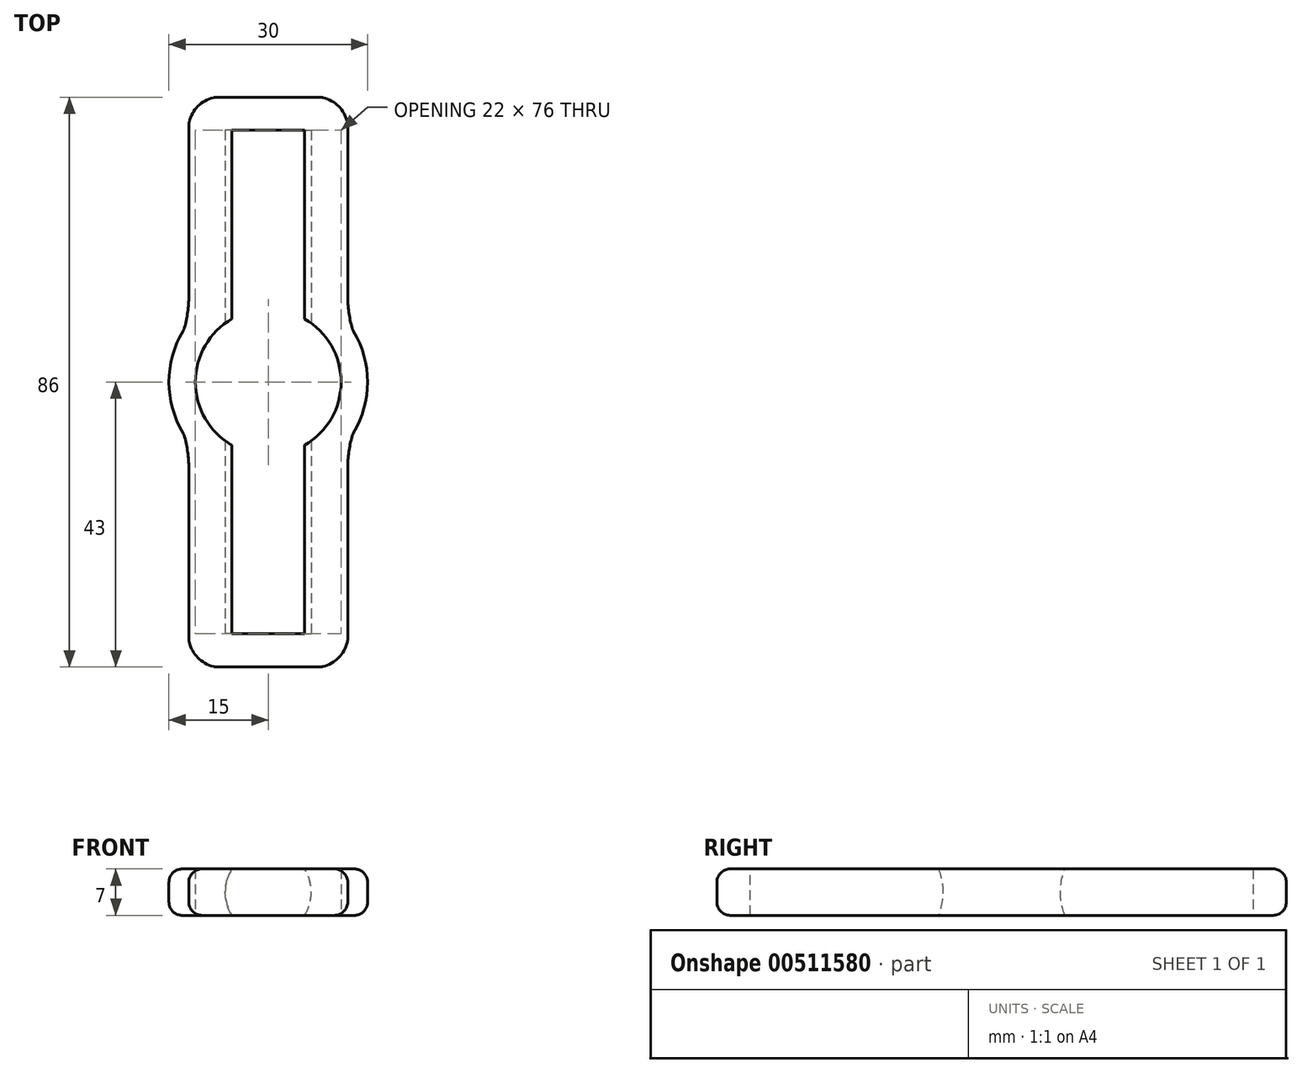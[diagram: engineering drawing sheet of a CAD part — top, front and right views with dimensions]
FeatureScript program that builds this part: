
annotation { "Feature Type Name" : "Feature", "Feature Type Description" : "" }
export const myFeature = defineFeature(function(context is Context, id is Id, definition is map)
    precondition{}
    {
        {
            var Q0;
            Q0=qCreatedBy(makeId("Top.planeOp"),FACE);
            var sketch = newSketch(context, id + "F0", { "sketchPlane" : qUnion([Q0])});
            skCircle(sketch, "E0", {"center": v(0, 0) * mm, "radius": 11 * mm});
            skCircle(sketch, "E1.0", {"center": v(0, 0) * mm, "radius": 15 * mm});
            skLineSegment(sketch, "E2", {"start": v(0, 11) * mm, "end": v(0, 15) * mm});
            skLineSegment(sketch, "E3", {"start": v(-12, 13) * mm, "end": v(-12, 39) * mm});
            skLineSegment(sketch, "E4", {"start": v(12, 13) * mm, "end": v(12, 39) * mm});
            skLineSegment(sketch, "E5", {"start": v(-8, 43) * mm, "end": v(-4, 43) * mm});
            skArc(sketch, "E6", {"start": v(-12.74, 7.92) * mm, "mid": v(-12.19, 10.43) * mm, "end": v(-12, 13) * mm});
            skArc(sketch, "E7.MirrorCS", {"start": v(12.74, 7.92) * mm, "mid": v(12.19, 10.43) * mm, "end": v(12, 13) * mm});
            skPoint(sketch, "E8.orphan", {"position": v(0, 13) * mm});
            skLineSegment(sketch, "E9.MirrorCS", {"start": v(12, -13) * mm, "end": v(12, -39) * mm});
            skLineSegment(sketch, "E10.MirrorCS", {"start": v(-8, -43) * mm, "end": v(8, -43) * mm});
            skLineSegment(sketch, "E11.MirrorCS", {"start": v(-12, -13) * mm, "end": v(-12, -39) * mm});
            skArc(sketch, "E12.MirrorCS", {"start": v(12.74, -7.92) * mm, "mid": v(12.19, -10.43) * mm, "end": v(12, -13) * mm});
            skArc(sketch, "E13.MirrorCS", {"start": v(-12.74, -7.92) * mm, "mid": v(-12.19, -10.43) * mm, "end": v(-12, -13) * mm});
            skLineSegment(sketch, "E14", {"start": v(4, 43) * mm, "end": v(4, 14.46) * mm});
            skPoint(sketch, "E15.start.orphan", {"position": v(0, 50.01) * mm});
            skLineSegment(sketch, "E16.MirrorCS", {"start": v(-4, 43) * mm, "end": v(-4, 14.46) * mm});
            skLineSegment(sketch, "E17.MirrorCS", {"start": v(-4, -43) * mm, "end": v(-4, -14.46) * mm});
            skLineSegment(sketch, "E18.MirrorCS", {"start": v(4, -43) * mm, "end": v(4, -14.46) * mm});
            skLineSegment(sketch, "E19.trimOffspring", {"start": v(4, 43) * mm, "end": v(8, 43) * mm});
            skPoint(sketch, "E20", {"position": v(8, 43) * mm});
            skPoint(sketch, "E21", {"position": v(12, 39) * mm});
            skArc(sketch, "E22", {"start": v(12, 39) * mm, "mid": v(10.62, 41.62) * mm, "end": v(8, 43) * mm});
            skPoint(sketch, "E23.orphan", {"position": v(12, 43) * mm});
            skArc(sketch, "E24.MirrorCS", {"start": v(-12, 39) * mm, "mid": v(-10.62, 41.62) * mm, "end": v(-8, 43) * mm});
            skArc(sketch, "E25.MirrorCS", {"start": v(12, -39) * mm, "mid": v(10.62, -41.62) * mm, "end": v(8, -43) * mm});
            skArc(sketch, "E26.MirrorCS", {"start": v(-12, -39) * mm, "mid": v(-10.62, -41.62) * mm, "end": v(-8, -43) * mm});
            skPoint(sketch, "E27.orphan", {"position": v(-12, 43) * mm});
            skPoint(sketch, "E28.orphan", {"position": v(12, -43) * mm});
            skPoint(sketch, "E29.orphan", {"position": v(-12, -43) * mm});
            skLineSegment(sketch, "E30", {"start": v(-4, 43) * mm, "end": v(4, 43) * mm});
            skSolve(sketch);
        }
        {
            var Q0;
            {var subQ1=sQuery(id+"F0.wireOp",EDGE,"E3");Q0=makeQuery(id+"F0.imprint","IMPRINT",FACE,{"disambiguationData":[TD([[makeQuery(id+"F0.imprint","IMPRINT",EDGE,{"derivedFrom":subQ1}),-1.0]])]});}
            var Q1;
            {var subQ1=sQuery(id+"F0.wireOp",EDGE,"E4");Q1=makeQuery(id+"F0.imprint","IMPRINT",FACE,{"disambiguationData":[TD([[makeQuery(id+"F0.imprint","IMPRINT",EDGE,{"derivedFrom":subQ1}),1.0]])]});}
            var Q2;
            {var subQ0=sQuery(id+"F0.wireOp",EDGE,"E14");Q2=makeQuery(id+"F0.imprint","IMPRINT",FACE,{"disambiguationData":[TD([[makeQuery(id+"F0.imprint","IMPRINT",EDGE,{"derivedFrom":subQ0}),-1.0]])]});}
            var Q3;
            Q3=makeQuery(id+"F0.imprint","IMPRINT",FACE,{"disambiguationData":[TD([[makeQuery(id+"F0.imprint","IMPRINT",EDGE,{"derivedFrom":sQuery(id+"F0.wireOp",EDGE,"E0")}),-1.0]])]});
            var Q4;
            {var subQ1=sQuery(id+"F0.wireOp",EDGE,"E9.MirrorCS");Q4=makeQuery(id+"F0.imprint","IMPRINT",FACE,{"disambiguationData":[TD([[makeQuery(id+"F0.imprint","IMPRINT",EDGE,{"derivedFrom":subQ1}),-1.0]])]});}
            var Q5;
            {var subQ0=sQuery(id+"F0.wireOp",EDGE,"E17.MirrorCS");Q5=makeQuery(id+"F0.imprint","IMPRINT",FACE,{"disambiguationData":[TD([[makeQuery(id+"F0.imprint","IMPRINT",EDGE,{"derivedFrom":subQ0}),-1.0]])]});}
            var Q6;
            {var subQ1=sQuery(id+"F0.wireOp",EDGE,"E11.MirrorCS");Q6=makeQuery(id+"F0.imprint","IMPRINT",FACE,{"disambiguationData":[TD([[makeQuery(id+"F0.imprint","IMPRINT",EDGE,{"derivedFrom":subQ1}),1.0]])]});}
            extrude(context, id + "F1", {"entities" : qUnion([Q0, Q1, Q2, Q3, Q4, Q5, Q6]), "endBound" : BoundingType.SYMMETRIC, "depth" : 7 * mm});
        }
        {
            var Q0;
            Q0=qCreatedBy(makeId("Front.planeOp"),FACE);
            var sketch = newSketch(context, id + "F2", { "sketchPlane" : qUnion([Q0])});
            skCircle(sketch, "E31", {"center": v(0, 0) * mm, "radius": 6.5 * mm});
            skSolve(sketch);
        }
        {
            var Q0;
            Q0=makeQuery(id+"F2.imprint","IMPRINT",FACE,{"disambiguationData":[TD([[makeQuery(id+"F2.imprint","IMPRINT",EDGE,{"derivedFrom":sQuery(id+"F2.wireOp",EDGE,"E31")}),1.0]])]});
            extrude(context, id + "F3", {"entities" : qUnion([Q0]), "operationType" : NewBodyOperationType.REMOVE, "endBound" : BoundingType.SYMMETRIC, "oppositeDirection" : true, "depth" : 76 * mm});
        }
        {
            var Q0;
            Q0=makeQuery(id+"F1.opExtrude","SWEPT_FACE",FACE,{"disambiguationData":[OSD([sQuery(id+"F0.wireOp",EDGE,"E3")])]});
            var Q1;
            Q1=makeQuery(id+"F1.opExtrude","SWEPT_FACE",FACE,{"disambiguationData":[OSD([sQuery(id+"F0.wireOp",EDGE,"E6")])]});
            var Q2;
            {var subQ0=sQuery(id+"F0.wireOp",EDGE,"E1.0");Q2=makeQuery(id+"F1.opExtrude","SWEPT_FACE",FACE,{"disambiguationData":[OSD([subQ0]),TDD([makeQuery(id+"F0.imprint","IMPRINT",EDGE,{"disambiguationData":[TD([[makeQuery(id+"F0.imprint","INTERSECT",VERTEX,{"derivedFrom":[subQ0,sQuery(id+"F0.wireOp",EDGE,"E6")]}),-1.0]])],"derivedFrom":subQ0})])]});}
            var Q3;
            Q3=makeQuery(id+"F1.opExtrude","SWEPT_FACE",FACE,{"disambiguationData":[OSD([sQuery(id+"F0.wireOp",EDGE,"E13.MirrorCS")])]});
            var Q4;
            Q4=makeQuery(id+"F1.opExtrude","SWEPT_FACE",FACE,{"disambiguationData":[OSD([sQuery(id+"F0.wireOp",EDGE,"E11.MirrorCS")])]});
            var Q5;
            Q5=makeQuery(id+"F1.opExtrude","SWEPT_FACE",FACE,{"disambiguationData":[OSD([sQuery(id+"F0.wireOp",EDGE,"E26.MirrorCS")])]});
            var Q6;
            Q6=makeQuery(id+"F1.opExtrude","SWEPT_FACE",FACE,{"disambiguationData":[OSD([sQuery(id+"F0.wireOp",EDGE,"E10.MirrorCS")])]});
            var Q7;
            Q7=makeQuery(id+"F1.opExtrude","SWEPT_FACE",FACE,{"disambiguationData":[OSD([sQuery(id+"F0.wireOp",EDGE,"E25.MirrorCS")])]});
            var Q8;
            Q8=makeQuery(id+"F1.opExtrude","SWEPT_FACE",FACE,{"disambiguationData":[OSD([sQuery(id+"F0.wireOp",EDGE,"E9.MirrorCS")])]});
            var Q9;
            Q9=makeQuery(id+"F1.opExtrude","SWEPT_FACE",FACE,{"disambiguationData":[OSD([sQuery(id+"F0.wireOp",EDGE,"E12.MirrorCS")])]});
            var Q10;
            {var subQ0=sQuery(id+"F0.wireOp",EDGE,"E1.0");Q10=makeQuery(id+"F1.opExtrude","SWEPT_FACE",FACE,{"disambiguationData":[OSD([subQ0]),TDD([makeQuery(id+"F0.imprint","IMPRINT",EDGE,{"disambiguationData":[TD([[makeQuery(id+"F0.imprint","INTERSECT",VERTEX,{"derivedFrom":[subQ0,sQuery(id+"F0.wireOp",EDGE,"E7.MirrorCS")]}),1.0]])],"derivedFrom":subQ0})])]});}
            var Q11;
            Q11=makeQuery(id+"F1.opExtrude","SWEPT_FACE",FACE,{"disambiguationData":[OSD([sQuery(id+"F0.wireOp",EDGE,"E7.MirrorCS")])]});
            var Q12;
            Q12=makeQuery(id+"F1.opExtrude","SWEPT_FACE",FACE,{"disambiguationData":[OSD([sQuery(id+"F0.wireOp",EDGE,"E4")])]});
            var Q13;
            Q13=makeQuery(id+"F1.opExtrude","SWEPT_FACE",FACE,{"disambiguationData":[OSD([sQuery(id+"F0.wireOp",EDGE,"E22")])]});
            var Q14;
            Q14=makeQuery(id+"F1.opExtrude","SWEPT_FACE",FACE,{"disambiguationData":[OSD([sQuery(id+"F0.wireOp",EDGE,"E5"),sQuery(id+"F0.wireOp",EDGE,"E19.trimOffspring"),sQuery(id+"F0.wireOp",EDGE,"E30")])]});
            var Q15;
            Q15=makeQuery(id+"F1.opExtrude","SWEPT_FACE",FACE,{"disambiguationData":[OSD([sQuery(id+"F0.wireOp",EDGE,"E24.MirrorCS")])]});
            fillet(context, id + "F4", {"entities" : qUnion([Q0, Q1, Q2, Q3, Q4, Q5, Q6, Q7, Q8, Q9, Q10, Q11, Q12, Q13, Q14, Q15]), "radius" : 2 * mm, "tangentPropagation" : true, "allowEdgeOverflow" : false});
        }
    });
